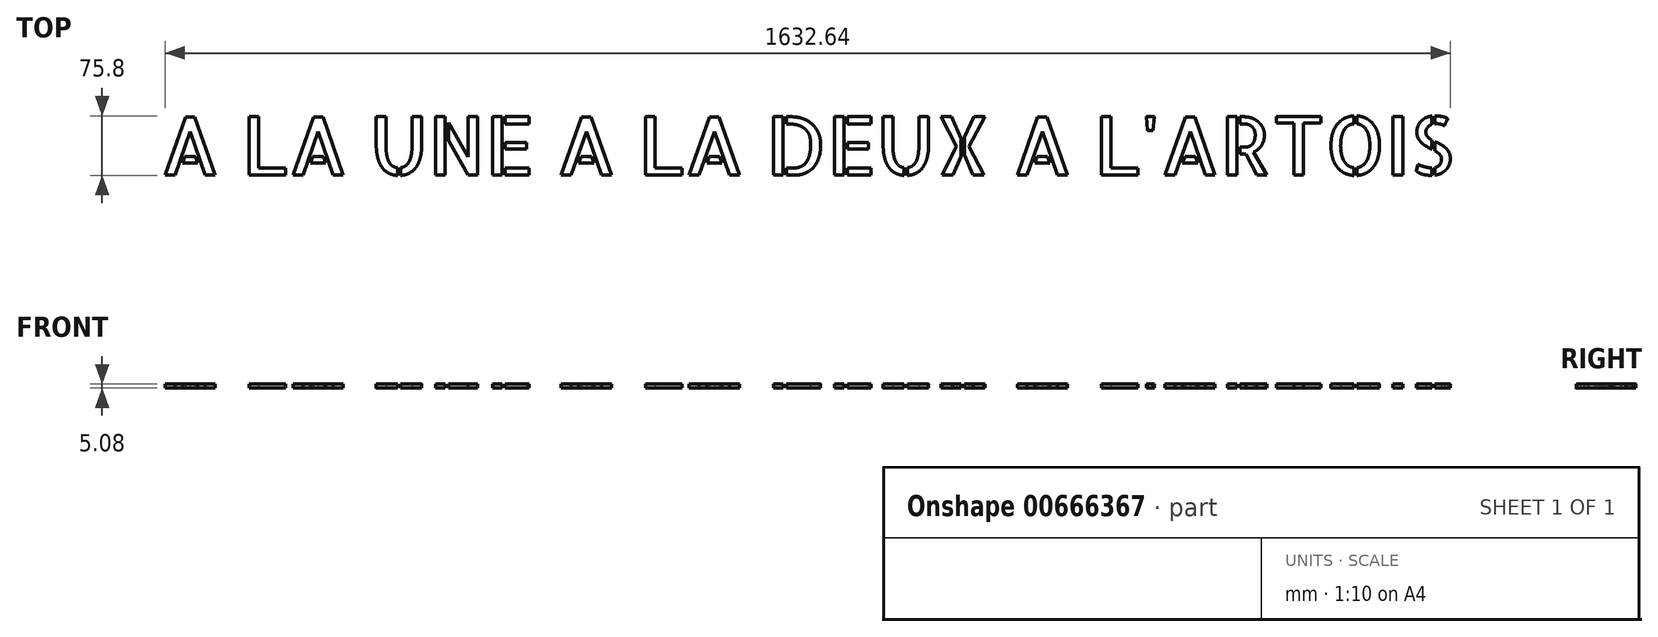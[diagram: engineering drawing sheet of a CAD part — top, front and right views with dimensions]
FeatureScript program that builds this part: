
annotation { "Feature Type Name" : "Feature", "Feature Type Description" : "" }
export const myFeature = defineFeature(function(context is Context, id is Id, definition is map)
    precondition{}
    {
        {
            var Q0;
            Q0=qCreatedBy(makeId("Top.planeOp"),FACE);
            var sketch = newSketch(context, id + "F0", { "sketchPlane" : qUnion([Q0])});
            skText(sketch, "E0", { "text": "A LA UNE A LA DEUX A L\'ARTOIS", "fontName": "AllertaStencil-Regular.ttf"});
            const initialGuessF0  = {"E0": [-0.01046, -0.07413, 1, 0, 0.07413]};
            skSetInitialGuess(sketch, initialGuessF0);
            skSolve(sketch);
        }
        {
            var Q0;
            Q0 = qSketchRegion(id + "F0", true);
            extrude(context, id + "F1", {"entities" : qUnion([Q0]), "depth" : 5.08 * mm, "offsetDistance" : 25.4 * mm});
        }
    });
